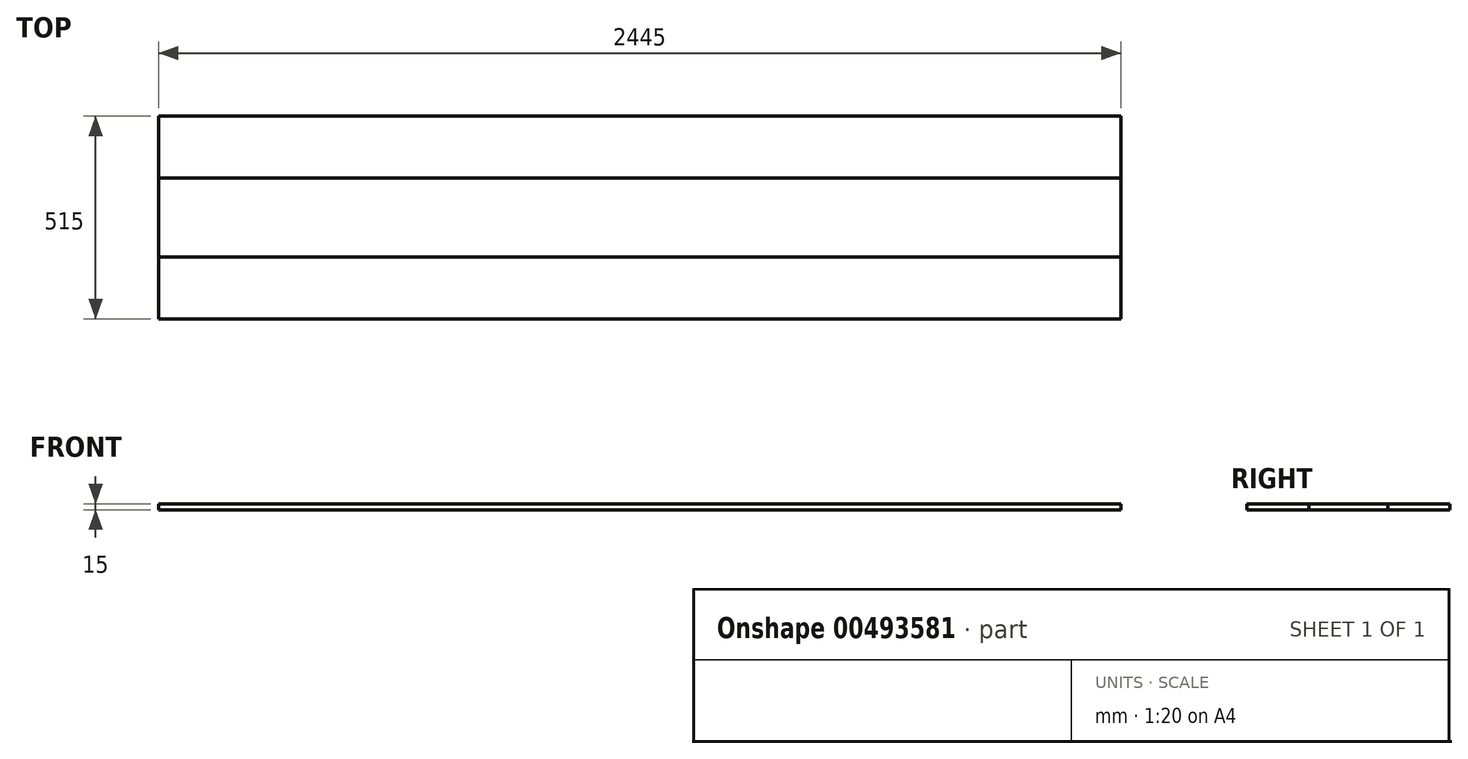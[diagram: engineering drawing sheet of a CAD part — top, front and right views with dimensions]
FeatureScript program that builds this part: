
annotation { "Feature Type Name" : "Feature", "Feature Type Description" : "" }
export const myFeature = defineFeature(function(context is Context, id is Id, definition is map)
    precondition{}
    {
        {
            var Q0;
            Q0=qCreatedBy(makeId("Top.planeOp"),FACE);
            var sketch = newSketch(context, id + "F0", { "sketchPlane" : qUnion([Q0])});
            skLineSegment(sketch, "E0.bottom", {"start": v(1222.5, 257.5) * mm, "end": v(-1222.5, 257.5) * mm});
            skLineSegment(sketch, "E0.top", {"start": v(1222.5, -257.5) * mm, "end": v(-1222.5, -257.5) * mm});
            skLineSegment(sketch, "E0.left", {"start": v(1222.5, 257.5) * mm, "end": v(1222.5, -257.5) * mm});
            skLineSegment(sketch, "E0.right", {"start": v(-1222.5, 257.5) * mm, "end": v(-1222.5, -257.5) * mm});
            skPoint(sketch, "E0.middle", {"position": v(0, 0) * mm});
            skSolve(sketch);
        }
        {
            var Q0;
            Q0=makeQuery(id+"F0.imprint","IMPRINT",FACE,{"disambiguationData":[TD([[makeQuery(id+"F0.imprint","IMPRINT",EDGE,{"derivedFrom":sQuery(id+"F0.wireOp",EDGE,"E0.bottom")}),1.0]])]});
            extrude(context, id + "F1", {"entities" : qUnion([Q0]), "endBound" : BoundingType.SYMMETRIC, "depth" : 15 * mm});
        }
        {
            var Q0;
            Q0=qCreatedBy(makeId("Top.planeOp"),FACE);
            var sketch = newSketch(context, id + "F2", { "sketchPlane" : qUnion([Q0])});
            skLineSegment(sketch, "E1.bottom", {"start": v(1222.5, 100) * mm, "end": v(-1222.5, 100) * mm});
            skLineSegment(sketch, "E1.top", {"start": v(1222.5, -100) * mm, "end": v(-1222.5, -100) * mm});
            skLineSegment(sketch, "E1.left", {"start": v(1222.5, 100) * mm, "end": v(1222.5, -100) * mm});
            skLineSegment(sketch, "E1.right", {"start": v(-1222.5, 100) * mm, "end": v(-1222.5, -100) * mm});
            skPoint(sketch, "E1.middle", {"position": v(0, 0) * mm});
            skSolve(sketch);
        }
        {
            var Q0;
            Q0=makeQuery(id+"F2.imprint","IMPRINT",FACE,{"disambiguationData":[TD([[makeQuery(id+"F2.imprint","IMPRINT",EDGE,{"derivedFrom":sQuery(id+"F2.wireOp",EDGE,"E1.bottom")}),1.0]])]});
            extrude(context, id + "F3", {"entities" : qUnion([Q0]), "endBound" : BoundingType.SYMMETRIC, "depth" : 15 * mm});
        }
    });
